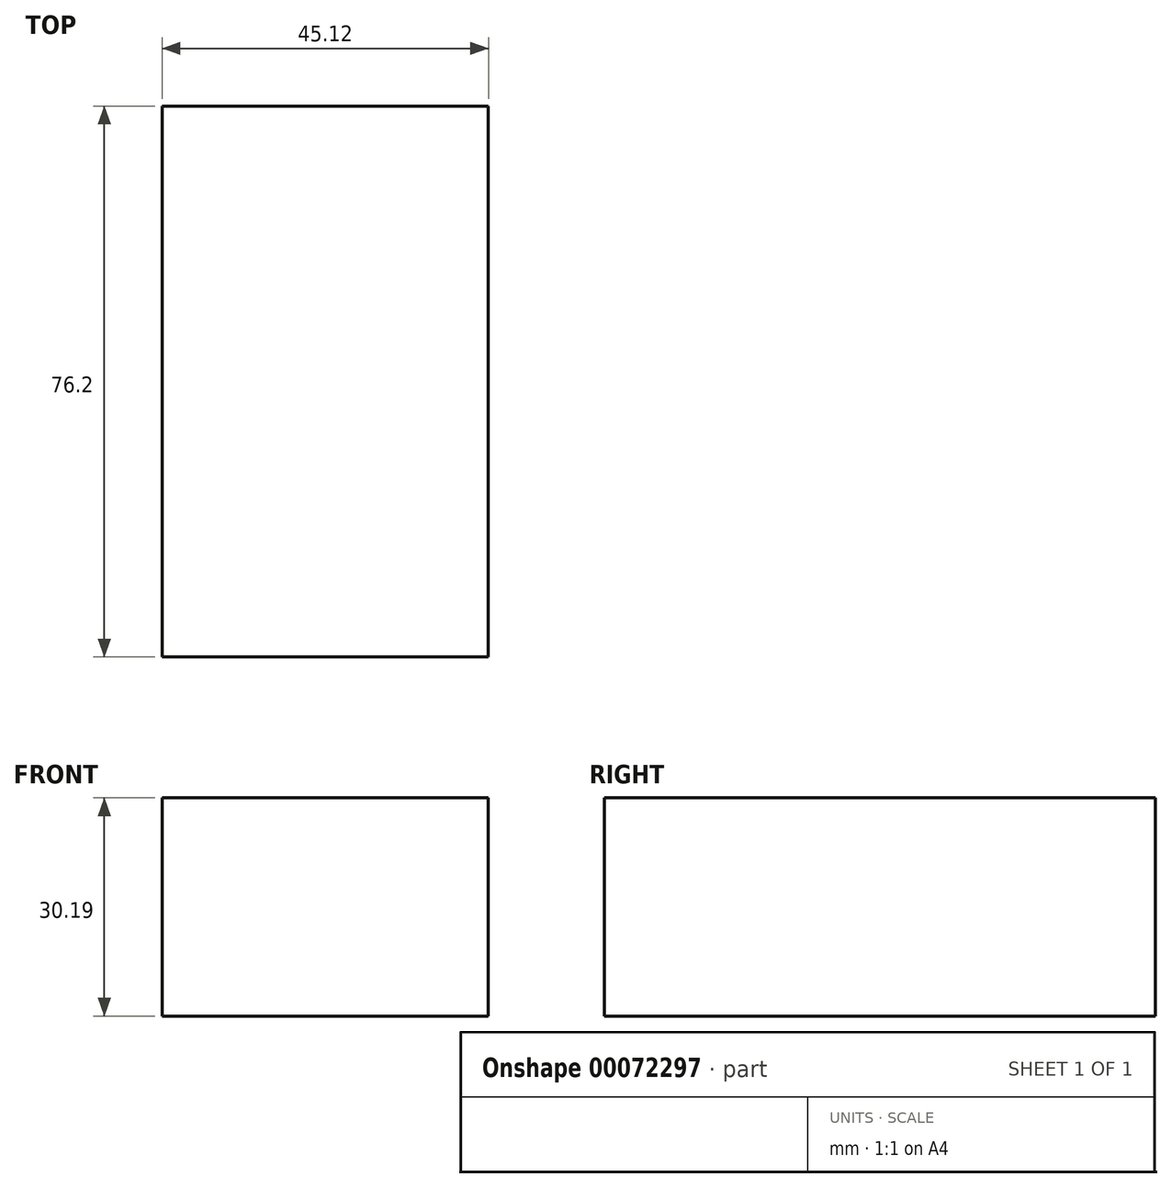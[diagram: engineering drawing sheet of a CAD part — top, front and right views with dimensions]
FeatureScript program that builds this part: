
annotation { "Feature Type Name" : "Feature", "Feature Type Description" : "" }
export const myFeature = defineFeature(function(context is Context, id is Id, definition is map)
    precondition{}
    {
        {
            var Q0;
            Q0=qCreatedBy(makeId("Front.planeOp"),FACE);
            var sketch = newSketch(context, id + "F0", { "sketchPlane" : qUnion([Q0])});
            skLineSegment(sketch, "E0.bottom", {"start": v(0, 0) * mm, "end": v(45.12, 0) * mm});
            skLineSegment(sketch, "E0.top", {"start": v(0, 30.2) * mm, "end": v(45.12, 30.2) * mm});
            skLineSegment(sketch, "E0.left", {"start": v(0, 0) * mm, "end": v(0, 30.2) * mm});
            skLineSegment(sketch, "E0.right", {"start": v(45.12, 0) * mm, "end": v(45.12, 30.2) * mm});
            skSolve(sketch);
        }
        {
            var Q0;
            Q0 = qSketchRegion(id + "F0", true);
            extrude(context, id + "F1", {"entities" : qUnion([Q0]), "depth" : 76.2 * mm});
        }
    });
